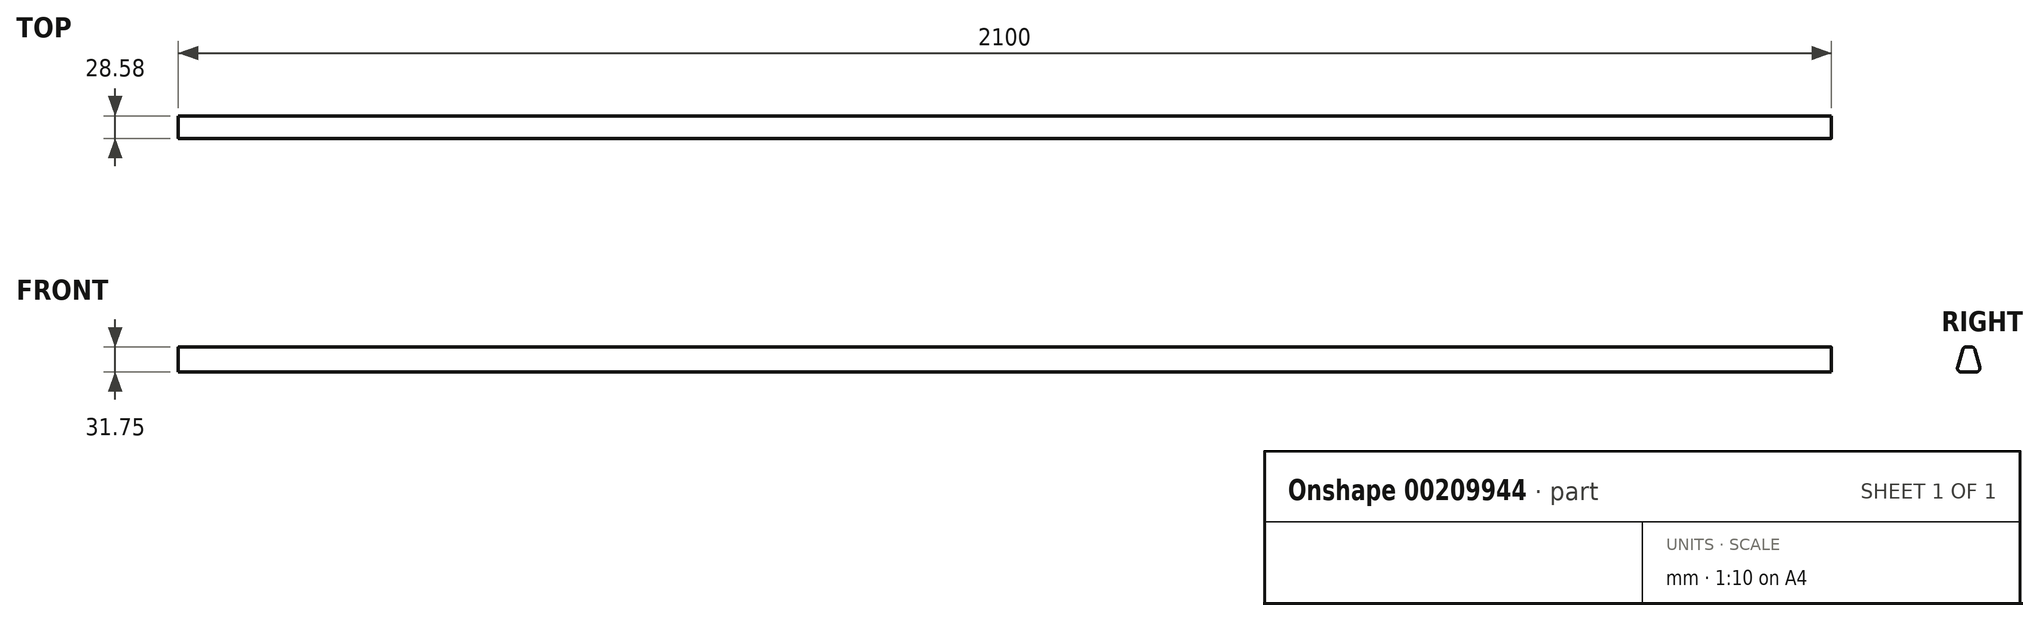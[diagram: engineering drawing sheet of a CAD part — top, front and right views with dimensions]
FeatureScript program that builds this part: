
annotation { "Feature Type Name" : "Feature", "Feature Type Description" : "" }
export const myFeature = defineFeature(function(context is Context, id is Id, definition is map)
    precondition{}
    {
        {
            var Q0;
            Q0=qCreatedBy(makeId("Right.planeOp"),FACE);
            var sketch = newSketch(context, id + "F0", { "sketchPlane" : qUnion([Q0])});
            skLineSegment(sketch, "E0", {"start": v(-9.32, 0) * mm, "end": v(9.32, 0) * mm});
            skLineSegment(sketch, "E1", {"start": v(14.09, 6.35) * mm, "end": v(7.62, 28.58) * mm});
            skLineSegment(sketch, "E2", {"start": v(3.39, 31.75) * mm, "end": v(-3.39, 31.75) * mm});
            skLineSegment(sketch, "E3", {"start": v(-7.62, 28.58) * mm, "end": v(-14.09, 6.35) * mm});
            skPoint(sketch, "E4.visualSharp", {"position": v(-6.7, 31.75) * mm});
            skArc(sketch, "E4.filletArc", {"start": v(-3.39, 31.75) * mm, "mid": v(-6.03, 30.87) * mm, "end": v(-7.62, 28.57) * mm});
            skPoint(sketch, "E5.visualSharp", {"position": v(6.7, 31.75) * mm});
            skArc(sketch, "E5.filletArc", {"start": v(7.62, 28.57) * mm, "mid": v(6.03, 30.87) * mm, "end": v(3.39, 31.75) * mm});
            skPoint(sketch, "E6.visualSharp", {"position": v(15.94, 0) * mm});
            skArc(sketch, "E6.filletArc", {"start": v(9.32, 0) * mm, "mid": v(13.3, 1.98) * mm, "end": v(14.09, 6.35) * mm});
            skPoint(sketch, "E7.visualSharp", {"position": v(-15.94, 0) * mm});
            skArc(sketch, "E7.filletArc", {"start": v(-14.09, 6.35) * mm, "mid": v(-13.3, 1.98) * mm, "end": v(-9.32, 0) * mm});
            skSolve(sketch);
        }
        {
            var Q0;
            Q0 = qSketchRegion(id + "F0", true);
            extrude(context, id + "F1", {"entities" : qUnion([Q0]), "endBound" : BoundingType.SYMMETRIC, "depth" : 2100 * mm});
        }
    });
